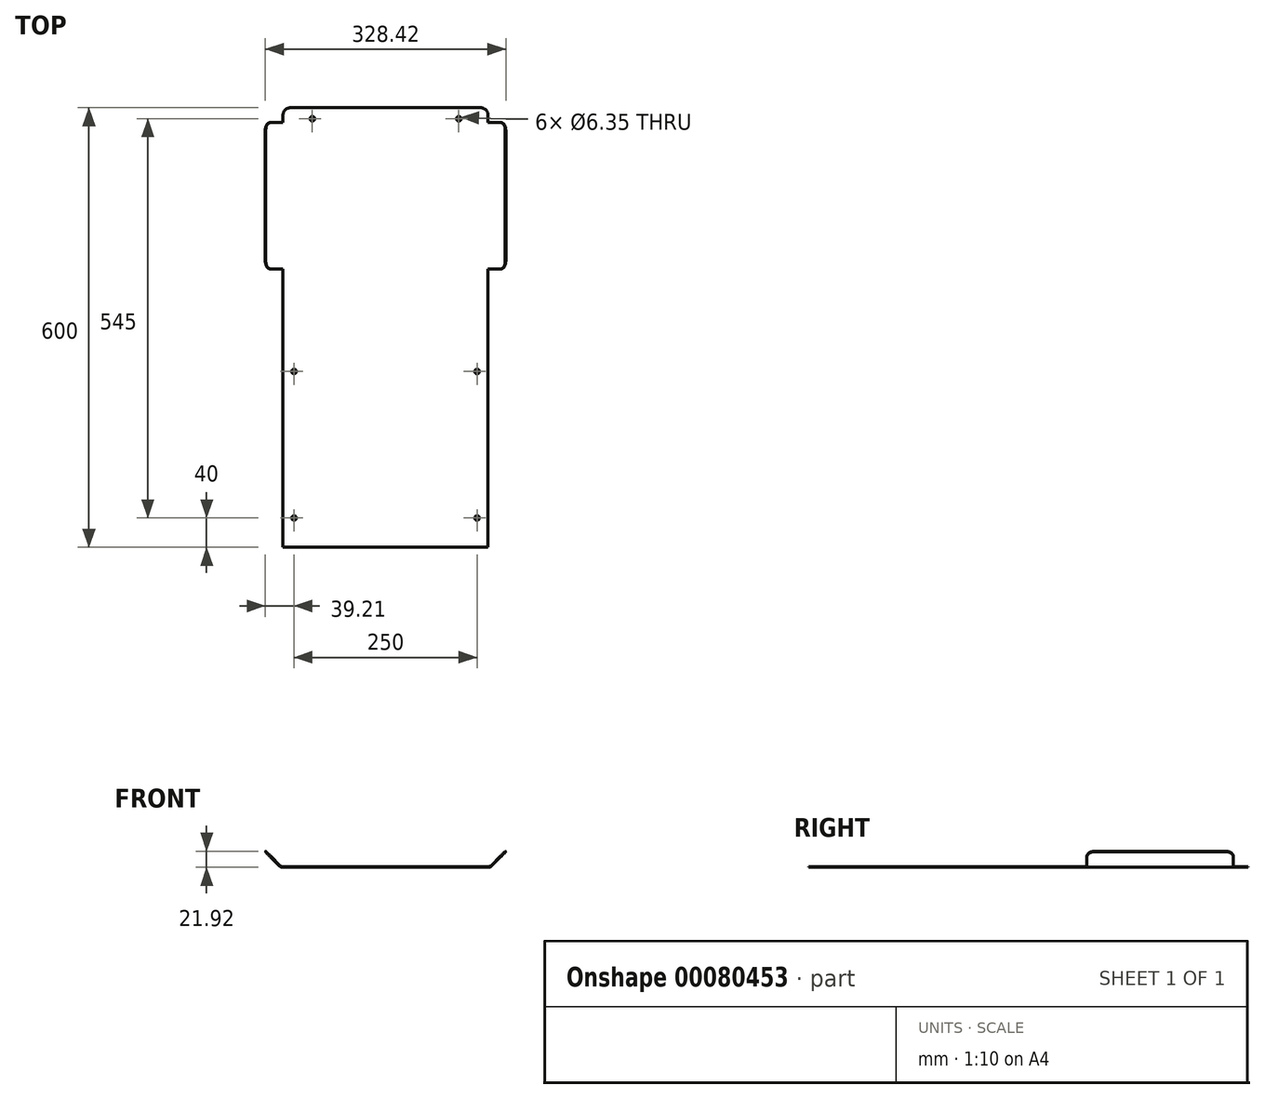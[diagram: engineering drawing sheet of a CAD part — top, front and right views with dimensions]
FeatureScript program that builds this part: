
annotation { "Feature Type Name" : "Feature", "Feature Type Description" : "" }
export const myFeature = defineFeature(function(context is Context, id is Id, definition is map)
    precondition{}
    {
        {
            var Q0;
            Q0=qCreatedBy(makeId("Top.planeOp"),FACE);
            var sketch = newSketch(context, id + "F0", { "sketchPlane" : qUnion([Q0])});
            skLineSegment(sketch, "E0.bottom", {"start": v(140, -300) * mm, "end": v(-140, -300) * mm});
            skLineSegment(sketch, "E0.top", {"start": v(140, 300) * mm, "end": v(-140, 300) * mm});
            skLineSegment(sketch, "E0.left", {"start": v(140, -300) * mm, "end": v(140, 300) * mm});
            skLineSegment(sketch, "E0.right", {"start": v(-140, -300) * mm, "end": v(-140, 300) * mm});
            skPoint(sketch, "E0.middle", {"position": v(0, 0) * mm});
            skSolve(sketch);
        }
        {
            var Q0;
            Q0 = qSketchRegion(id + "F0", true);
            extrude(context, id + "F1", {"entities" : qUnion([Q0]), "depth" : 1 * mm});
        }
        {
            var Q0;
            Q0=makeQuery(id+"F1.opExtrude","SWEPT_FACE",FACE,{"disambiguationData":[OSD([sQuery(id+"F0.wireOp",EDGE,"E0.top")])]});
            cPlane(context, id + "F2", {"entities" : qUnion([Q0]), "cplaneType" : CPlaneType.OFFSET, "offset" : 20 * mm, "oppositeDirection" : true, "width" : 150 * mm, "height" : 150 * mm});
        }
        {
            var Q0;
            Q0=qCreatedBy(id+"F2.planeOp",FACE);
            var sketch = newSketch(context, id + "F3", { "sketchPlane" : qUnion([Q0])});
            skLineSegment(sketch, "E1", {"start": v(-140, 1) * mm, "end": v(-140, 0) * mm});
            skLineSegment(sketch, "E2", {"start": v(-140, 0) * mm, "end": v(-140.93, 0) * mm});
            skLineSegment(sketch, "E3", {"start": v(-144.46, 1.46) * mm, "end": v(-164.21, 21.21) * mm});
            skLineSegment(sketch, "E4", {"start": v(-164.21, 21.21) * mm, "end": v(-163.5, 21.92) * mm});
            skLineSegment(sketch, "E5", {"start": v(-163.5, 21.92) * mm, "end": v(-144.05, 2.46) * mm});
            skLineSegment(sketch, "E6", {"start": v(-140.51, 1) * mm, "end": v(-140, 1) * mm});
            skPoint(sketch, "E7.visualSharp", {"position": v(-143, 0) * mm});
            skArc(sketch, "E7.filletArc", {"start": v(-144.46, 1.46) * mm, "mid": v(-142.84, 0.38) * mm, "end": v(-140.93, 0) * mm});
            skPoint(sketch, "E8.visualSharp", {"position": v(-142.59, 1) * mm});
            skArc(sketch, "E8.filletArc", {"start": v(-144.05, 2.46) * mm, "mid": v(-142.43, 1.38) * mm, "end": v(-140.51, 1) * mm});
            skSolve(sketch);
        }
        {
            var Q0;
            Q0 = qSketchRegion(id + "F3", true);
            extrude(context, id + "F4", {"entities" : qUnion([Q0]), "oppositeDirection" : true, "depth" : 200 * mm});
        }
        {
            var Q0;
            Q0=makeQuery(id+"F4.opExtrude","SWEPT_BODY",BODY,{"disambiguationData":[OSD([sQuery(id+"F3.wireOp",EDGE,"E1"),sQuery(id+"F3.wireOp",EDGE,"E2"),sQuery(id+"F3.wireOp",EDGE,"E3"),sQuery(id+"F3.wireOp",EDGE,"E4"),sQuery(id+"F3.wireOp",EDGE,"E5"),sQuery(id+"F3.wireOp",EDGE,"E6"),sQuery(id+"F3.wireOp",EDGE,"E7.filletArc"),sQuery(id+"F3.wireOp",EDGE,"E8.filletArc")])]});
            var Q1;
            Q1=qCreatedBy(makeId("Right.planeOp"),FACE);
            mirror(context, id + "F5", {"operationType" : NewBodyOperationType.ADD, "entities" : qUnion([Q0]), "mirrorPlane" : qUnion([Q1])});
        }
        {
            var Q0;
            Q0=makeQuery(id+"F1.opExtrude","SWEPT_EDGE",EDGE,{"disambiguationData":[OSD([sQuery(id+"F0.wireOp",EDGE,"E0.top"),sQuery(id+"F0.wireOp",EDGE,"E0.left")])]});
            var Q1;
            Q1=makeQuery(id+"F4.opExtrude","CAP_EDGE",EDGE,{"disambiguationData":[OSD([sQuery(id+"F3.wireOp",EDGE,"E1")])],"isStart":true});
            var Q2;
            Q2=makeQuery(id+"F4.opExtrude","CAP_EDGE",EDGE,{"disambiguationData":[OSD([sQuery(id+"F3.wireOp",EDGE,"E4")])],"isStart":true});
            var Q3;
            Q3=makeQuery(id+"F4.opExtrude","CAP_EDGE",EDGE,{"disambiguationData":[OSD([sQuery(id+"F3.wireOp",EDGE,"E4")])],"isStart":false});
            var Q4;
            Q4=makeQuery(id+"F4.opExtrude","CAP_EDGE",EDGE,{"disambiguationData":[OSD([sQuery(id+"F3.wireOp",EDGE,"E1")])],"isStart":false});
            var Q5;
            Q5=makeQuery(id+"F5.opPattern","COPY",EDGE,{"derivedFrom":makeQuery(id+"F4.opExtrude","CAP_EDGE",EDGE,{"disambiguationData":[OSD([sQuery(id+"F3.wireOp",EDGE,"E1")])],"isStart":false}),"instanceName":"1"});
            var Q6;
            Q6=makeQuery(id+"F5.opPattern","COPY",EDGE,{"derivedFrom":makeQuery(id+"F4.opExtrude","CAP_EDGE",EDGE,{"disambiguationData":[OSD([sQuery(id+"F3.wireOp",EDGE,"E4")])],"isStart":false}),"instanceName":"1"});
            var Q7;
            Q7=makeQuery(id+"F5.opPattern","COPY",EDGE,{"derivedFrom":makeQuery(id+"F4.opExtrude","CAP_EDGE",EDGE,{"disambiguationData":[OSD([sQuery(id+"F3.wireOp",EDGE,"E4")])],"isStart":true}),"instanceName":"1"});
            var Q8;
            Q8=makeQuery(id+"F5.opPattern","COPY",EDGE,{"derivedFrom":makeQuery(id+"F4.opExtrude","CAP_EDGE",EDGE,{"disambiguationData":[OSD([sQuery(id+"F3.wireOp",EDGE,"E1")])],"isStart":true}),"instanceName":"1"});
            var Q9;
            Q9=makeQuery(id+"F1.opExtrude","SWEPT_EDGE",EDGE,{"disambiguationData":[OSD([sQuery(id+"F0.wireOp",EDGE,"E0.top"),sQuery(id+"F0.wireOp",EDGE,"E0.right")])]});
            fillet(context, id + "F6", {"entities" : qUnion([Q0, Q1, Q2, Q3, Q4, Q5, Q6, Q7, Q8, Q9]), "radius" : 10 * mm, "tangentPropagation" : true, "allowEdgeOverflow" : false});
        }
        {
            var Q0;
            {var subQ0=makeQuery(id+"F4.opExtrude","SWEPT_FACE",FACE,{"disambiguationData":[OSD([sQuery(id+"F3.wireOp",EDGE,"E6")])]});Q0=makeQuery(id+"F5.boolean.opBoolean","MERGE",FACE,{"derivedFrom":[makeQuery(id+"F1.opExtrude","CAP_FACE",FACE,{"disambiguationData":[OSD([sQuery(id+"F0.wireOp",EDGE,"E0.bottom"),sQuery(id+"F0.wireOp",EDGE,"E0.top"),sQuery(id+"F0.wireOp",EDGE,"E0.left"),sQuery(id+"F0.wireOp",EDGE,"E0.right")])],"isStart":false}),subQ0,makeQuery(id+"F5.opPattern","COPY",FACE,{"derivedFrom":subQ0,"instanceName":"1"})]});}
            var sketch = newSketch(context, id + "F7", { "sketchPlane" : qUnion([Q0])});
            skCircle(sketch, "E9", {"center": v(-125, -260) * mm, "radius": 3.17 * mm});
            skCircle(sketch, "E10", {"center": v(-125, -60) * mm, "radius": 3.17 * mm});
            skCircle(sketch, "E11", {"center": v(125, -260) * mm, "radius": 3.17 * mm});
            skCircle(sketch, "E12", {"center": v(125, -60) * mm, "radius": 3.17 * mm});
            skCircle(sketch, "E13", {"center": v(-100, 285) * mm, "radius": 3.17 * mm});
            skCircle(sketch, "E14", {"center": v(100, 285) * mm, "radius": 3.17 * mm});
            skLineSegment(sketch, "E15", {"start": v(0, 0) * mm, "end": v(0, 394.67) * mm, "construction": true});
            skSolve(sketch);
        }
        {
            var Q0;
            Q0 = qSketchRegion(id + "F7", true);
            extrude(context, id + "F8", {"entities" : qUnion([Q0]), "operationType" : NewBodyOperationType.REMOVE, "endBound" : BoundingType.THROUGH_ALL, "oppositeDirection" : true, "depth" : 25 * mm});
        }
    });
